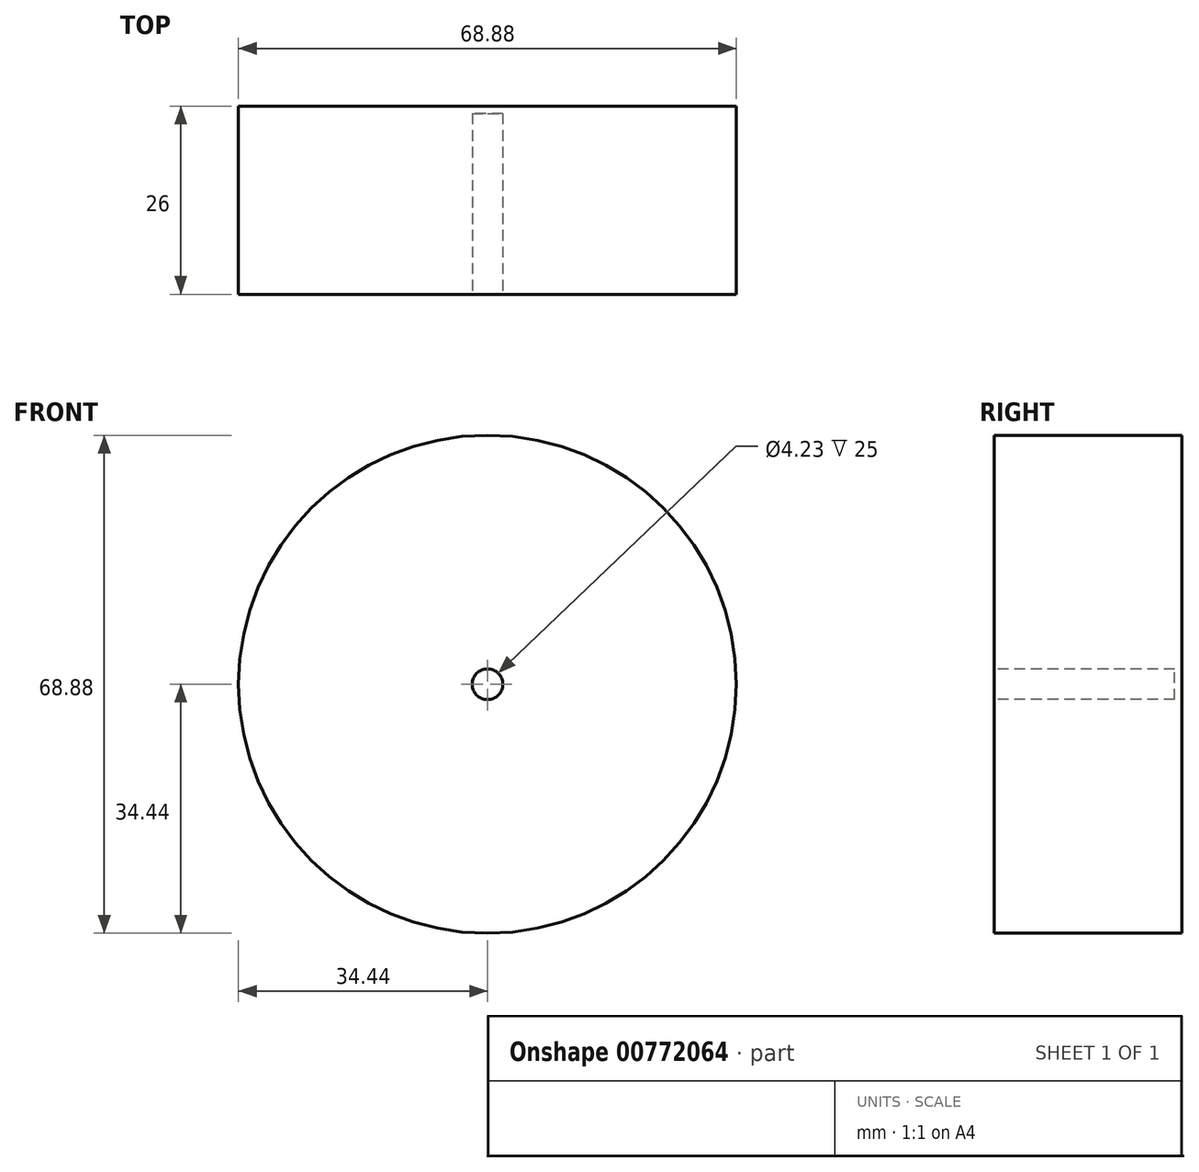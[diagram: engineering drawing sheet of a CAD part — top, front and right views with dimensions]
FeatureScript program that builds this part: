
annotation { "Feature Type Name" : "Feature", "Feature Type Description" : "" }
export const myFeature = defineFeature(function(context is Context, id is Id, definition is map)
    precondition{}
    {
        {
            var Q0;
            Q0=qCreatedBy(makeId("Front.planeOp"),FACE);
            var sketch = newSketch(context, id + "F0", { "sketchPlane" : qUnion([Q0])});
            skCircle(sketch, "E0", {"center": v(0, 0) * mm, "radius": 34.44 * mm});
            skSolve(sketch);
        }
        {
            var Q0;
            Q0 = qSketchRegion(id + "F0", true);
            var Q1;
            Q1=makeQuery(id+"F0.imprint","IMPRINT",FACE,{"disambiguationData":[TD([[makeQuery(id+"F0.imprint","IMPRINT",EDGE,{"derivedFrom":sQuery(id+"F0.wireOp",EDGE,"E0")}),1.0]])]});
            extrude(context, id + "F1", {"entities" : qUnion([Q0, Q1]), "depth" : 26 * mm, "offsetDistance" : 25 * mm});
        }
        {
            var Q0;
            Q0=makeQuery(id+"F1.opExtrude","CAP_FACE",FACE,{"disambiguationData":[OSD([sQuery(id+"F0.wireOp",EDGE,"E0")])],"isStart":false});
            var sketch = newSketch(context, id + "F2", { "sketchPlane" : qUnion([Q0])});
            skCircle(sketch, "E1", {"center": v(0, 0) * mm, "radius": 2.12 * mm});
            skSolve(sketch);
        }
        {
            var Q0;
            Q0=makeQuery(id+"F2.imprint","IMPRINT",FACE,{"disambiguationData":[TD([[makeQuery(id+"F2.imprint","IMPRINT",EDGE,{"derivedFrom":sQuery(id+"F2.wireOp",EDGE,"E1")}),1.0]])]});
            extrude(context, id + "F3", {"entities" : qUnion([Q0]), "operationType" : NewBodyOperationType.REMOVE, "oppositeDirection" : true, "depth" : 25 * mm, "offsetDistance" : 25 * mm});
        }
    });
